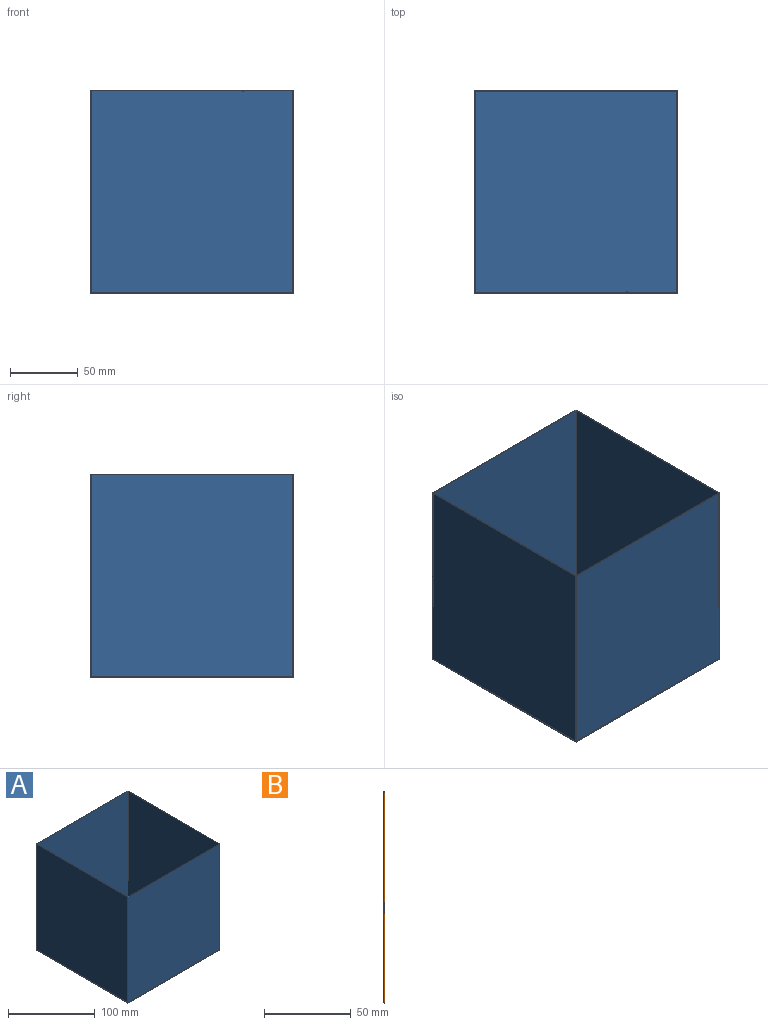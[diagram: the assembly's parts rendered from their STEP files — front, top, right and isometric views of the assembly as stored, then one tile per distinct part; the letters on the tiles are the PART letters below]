
ASSEMBLY  parts=2 mates=1
PART A: 11 faces, bbox 150x150x150 mm
  f0: plane 150x150mm, normal (0,0,1), area 299mm2, adj f1,f2,f3,f4,f6,f7,f8,f9
  f1: plane 150x150mm, normal (0,1,0), area 22500mm2, adj f0,f2,f4,f5
  f2: plane 150x150mm, normal (-1,0,0), area 22500mm2, adj f0,f1,f3,f5
  f3: plane 150x150mm, normal (0,-1,0), area 22500mm2, adj f0,f2,f4,f5
  f4: plane 150x150mm, normal (1,0,0), area 22500mm2, adj f0,f1,f3,f5
  f5: plane 150x150mm, normal (0,0,-1), area 22500mm2, adj f1,f2,f3,f4
  f6: plane 149.5x149mm, normal (0,-1,0), area 22275.5mm2, adj f0,f7,f9,f10
  f7: plane 149.5x149mm, normal (1,0,0), area 22275.5mm2, adj f0,f6,f8,f10
  f8: plane 149.5x149mm, normal (0,1,0), area 22275.5mm2, adj f0,f7,f9,f10
  f9: plane 149.5x149mm, normal (-1,0,0), area 22275.5mm2, adj f0,f6,f8,f10
  f10: plane 149x149mm, normal (0,0,1), area 22201mm2, adj f6,f7,f8,f9
PART B: 3 faces, bbox 1x1x149 mm
  f0: cylinder r=0.5mm len=149mm, axis (0,0,-1), area 468.1mm2, adj f1,f2
  f1: plane 1x1mm, normal (0,0,1), area 0.8mm2, adj f0
  f2: plane 1x1mm, normal (0,0,-1), area 0.8mm2, adj f0
PLACE A t=(317.84,-295.99,44.8)mm
PLACE B t=(355.68,-369.99,44.8)mm
MATE planar B.f0 <-> A.f10  axis (0,0,-1) through (355.68,-369.99,-29.7)mm
